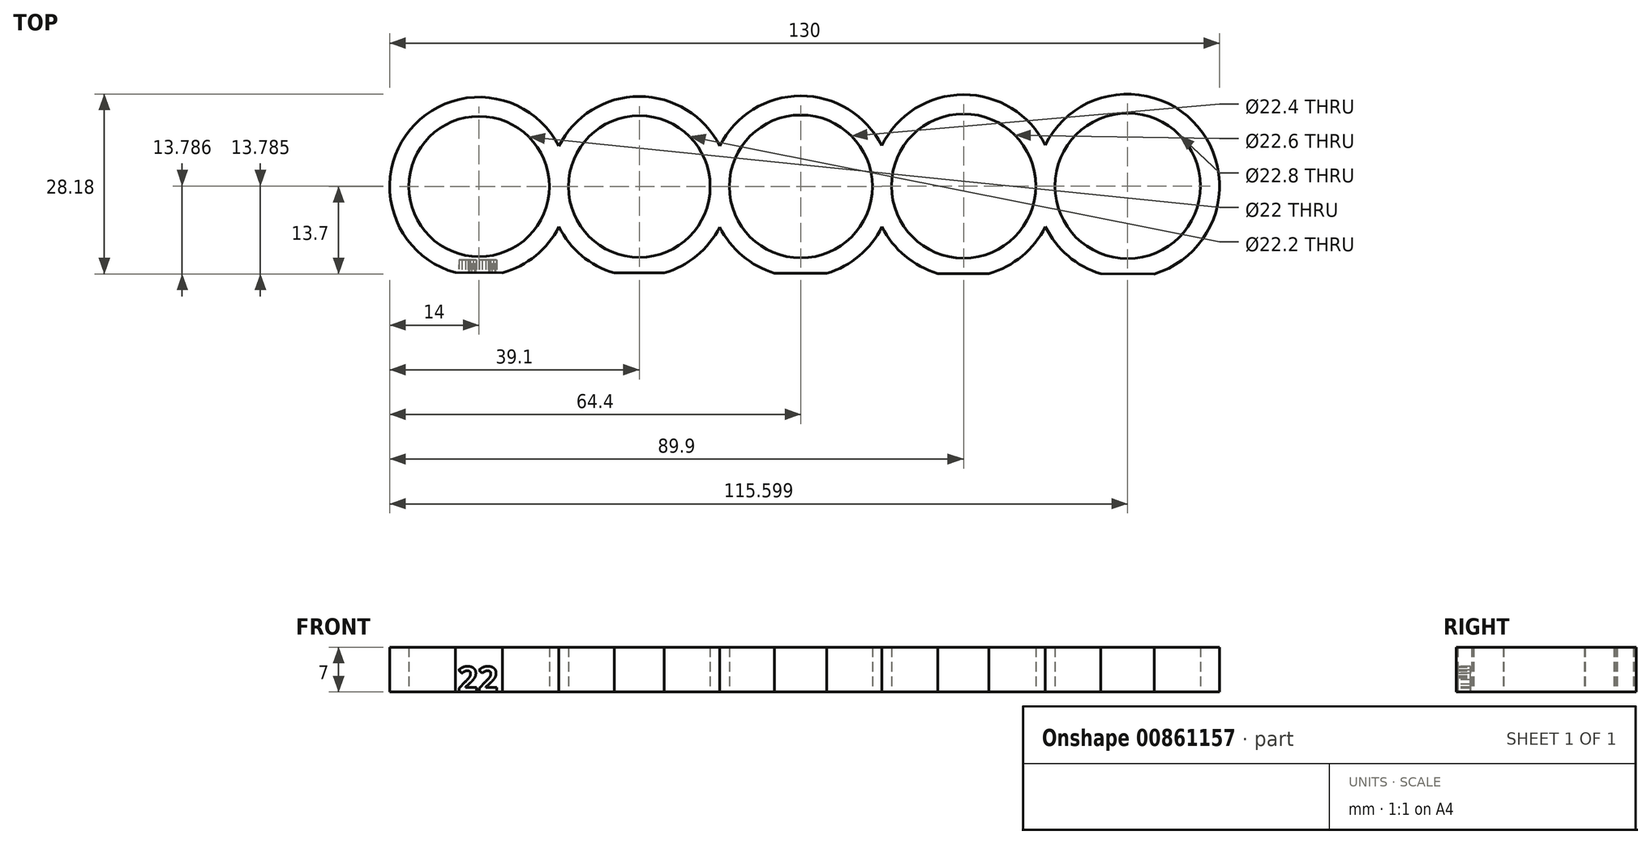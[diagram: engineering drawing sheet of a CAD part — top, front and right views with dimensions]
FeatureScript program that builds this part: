
annotation { "Feature Type Name" : "Feature", "Feature Type Description" : "" }
export const myFeature = defineFeature(function(context is Context, id is Id, definition is map)
    precondition{}
    {
        {
            var Q0;
            Q0=qCreatedBy(makeId("Top.planeOp"),FACE);
            var sketch = newSketch(context, id + "F0", { "sketchPlane" : qUnion([Q0])});
            skCircle(sketch, "E0", {"center": v(0, 0) * mm, "radius": 11.2 * mm});
            skCircle(sketch, "E1", {"center": v(25.5, 0.09) * mm, "radius": 11.3 * mm});
            skCircle(sketch, "E2", {"center": v(51.2, 0.08) * mm, "radius": 11.4 * mm});
            skCircle(sketch, "E3", {"center": v(-50.4, 0) * mm, "radius": 11 * mm});
            skCircle(sketch, "E4", {"center": v(-25.3, 0) * mm, "radius": 11.1 * mm});
            skLineSegment(sketch, "E5", {"start": v(-14.7, 0) * mm, "end": v(-14.2, 0) * mm, "construction": true});
            skLineSegment(sketch, "E6", {"start": v(-39.45, 0) * mm, "end": v(-39.4, 0) * mm, "construction": true});
            skLineSegment(sketch, "E7", {"start": v(39.8, 0) * mm, "end": v(40.1, 0) * mm, "construction": true});
            skArc(sketch, "E8.0", {"start": v(-37.9, 6.32) * mm, "mid": v(-64.4, 0) * mm, "end": v(-37.9, -6.32) * mm});
            skArc(sketch, "E9.0", {"start": v(-37.9, -6.32) * mm, "mid": v(-25.31, -14.1) * mm, "end": v(-12.7, -6.34) * mm});
            skArc(sketch, "E10.0", {"start": v(-12.7, -6.34) * mm, "mid": v(0.01, -14.2) * mm, "end": v(12.72, -6.32) * mm});
            skArc(sketch, "E11.0", {"start": v(11.2, 0.08) * mm, "mid": v(11.2, 0.04) * mm, "end": v(11.2, 0) * mm});
            skArc(sketch, "E12.0", {"start": v(36.8, 0.18) * mm, "mid": v(36.8, 0.09) * mm, "end": v(36.8, 0) * mm});
            skArc(sketch, "E13.trimOffspring", {"start": v(-12.7, 6.34) * mm, "mid": v(-25.31, 14.1) * mm, "end": v(-37.9, 6.32) * mm});
            skArc(sketch, "E14.trimOffspring", {"start": v(12.67, 6.4) * mm, "mid": v(-0.04, 14.2) * mm, "end": v(-12.7, 6.34) * mm});
            skPoint(sketch, "E15.start.orphan", {"position": v(11.2, 0) * mm});
            skArc(sketch, "E16.trimOffspring", {"start": v(12.72, -6.32) * mm, "mid": v(25.51, -14.21) * mm, "end": v(38.3, -6.3) * mm});
            skArc(sketch, "E17.trimOffspring", {"start": v(14.2, 0.01) * mm, "mid": v(14.2, 0.05) * mm, "end": v(14.2, 0.09) * mm});
            skArc(sketch, "E18.trimOffspring", {"start": v(38.3, 6.47) * mm, "mid": v(25.46, 14.39) * mm, "end": v(12.67, 6.4) * mm});
            skArc(sketch, "E19.trimOffspring", {"start": v(38.3, -6.3) * mm, "mid": v(65.6, 0.08) * mm, "end": v(38.3, 6.47) * mm});
            skArc(sketch, "E20.trimOffspring", {"start": v(39.8, 0) * mm, "mid": v(39.8, 0.09) * mm, "end": v(39.8, 0.18) * mm});
            skSolve(sketch);
        }
        {
            var Q0;
            Q0 = qSketchRegion(id + "F0", true);
            extrude(context, id + "F1", {"entities" : qUnion([Q0]), "depth" : 7 * mm, "offsetDistance" : 25 * mm});
        }
        {
            var Q0;
            Q0=makeQuery(id+"F1.opExtrude","CAP_FACE",FACE,{"disambiguationData":[OSD([sQuery(id+"F0.wireOp",EDGE,"E0"),sQuery(id+"F0.wireOp",EDGE,"E1"),sQuery(id+"F0.wireOp",EDGE,"E2"),sQuery(id+"F0.wireOp",EDGE,"E3"),sQuery(id+"F0.wireOp",EDGE,"E4"),sQuery(id+"F0.wireOp",EDGE,"E8.0"),sQuery(id+"F0.wireOp",EDGE,"E9.0"),sQuery(id+"F0.wireOp",EDGE,"E10.0"),sQuery(id+"F0.wireOp",EDGE,"E13.trimOffspring"),sQuery(id+"F0.wireOp",EDGE,"E14.trimOffspring"),sQuery(id+"F0.wireOp",EDGE,"E16.trimOffspring"),sQuery(id+"F0.wireOp",EDGE,"E18.trimOffspring"),sQuery(id+"F0.wireOp",EDGE,"E19.trimOffspring")])],"isStart":false});
            var sketch = newSketch(context, id + "F2", { "sketchPlane" : qUnion([Q0])});
            skLineSegment(sketch, "E21", {"start": v(-50.4, -14) * mm, "end": v(-50.4, -13.5) * mm, "construction": true});
            skLineSegment(sketch, "E22", {"start": v(-25.3, -14.1) * mm, "end": v(-25.3, -13.6) * mm, "construction": true});
            skPoint(sketch, "E22.startSnap0", {"position": v(-25.31, -14.1) * mm});
            skLineSegment(sketch, "E23", {"start": v(0.01, -14.2) * mm, "end": v(0.01, -13.7) * mm, "construction": true});
            skPoint(sketch, "E23.startSnap0", {"position": v(0.01, -14.2) * mm});
            skLineSegment(sketch, "E24", {"start": v(25.51, -14.21) * mm, "end": v(25.51, -13.71) * mm, "construction": true});
            skLineSegment(sketch, "E25", {"start": v(52.9, -14.21) * mm, "end": v(52.9, -13.71) * mm, "construction": true});
            skLineSegment(sketch, "E26", {"start": v(-50.4, -13.5) * mm, "end": v(63.83, -13.71) * mm});
            skLineSegment(sketch, "E27", {"start": v(-50.4, -13.5) * mm, "end": v(-55.8, -13.49) * mm});
            skLineSegment(sketch, "E28", {"start": v(-55.8, -13.49) * mm, "end": v(-55.8, -17.63) * mm});
            skLineSegment(sketch, "E29", {"start": v(-55.8, -17.63) * mm, "end": v(63.83, -17.85) * mm});
            skLineSegment(sketch, "E30", {"start": v(63.83, -17.85) * mm, "end": v(63.83, -13.71) * mm});
            skSolve(sketch);
        }
        {
            var Q0;
            Q0 = qSketchRegion(id + "F2", true);
            extrude(context, id + "F3", {"entities" : qUnion([Q0]), "operationType" : NewBodyOperationType.REMOVE, "oppositeDirection" : true, "depth" : 25 * mm, "offsetDistance" : 25 * mm});
        }
        {
            var Q0;
            {var subQ7=sQuery(id+"F0.wireOp",EDGE,"E8.0");Q0=makeQuery(id+"F3.boolean.opBoolean","COPY",FACE,{"disambiguationData":[TD([makeQuery(id+"F1.opExtrude","SWEPT_FACE",FACE,{"disambiguationData":[OSD([subQ7])]})])],"derivedFrom":makeQuery(id+"F3.opExtrude","SWEPT_FACE",FACE,{"disambiguationData":[OSD([sQuery(id+"F2.wireOp",EDGE,"E26"),sQuery(id+"F2.wireOp",EDGE,"E27")])]})});}
            var sketch = newSketch(context, id + "F4", { "sketchPlane" : qUnion([Q0])});
            skLineSegment(sketch, "E31.bottom", {"start": v(-41.37, -12.98) * mm, "end": v(-26.4, -12.98) * mm});
            skLineSegment(sketch, "E31.top", {"start": v(-41.37, -1.66) * mm, "end": v(-26.4, -1.66) * mm});
            skLineSegment(sketch, "E31.left", {"start": v(-41.37, -12.98) * mm, "end": v(-41.37, -1.66) * mm});
            skLineSegment(sketch, "E31.right", {"start": v(-26.4, -12.98) * mm, "end": v(-26.4, -1.66) * mm});
            skText(sketch, "E32", { "text": "22", "fontName": "OpenSans-Bold.ttf"});
            const initialGuessF4  = {"E32": [-0.05376, 0, 1, 0, 0.004]};
            skSetInitialGuess(sketch, initialGuessF4);
            skSolve(sketch);
        }
        {
            var Q0;
            Q0=makeQuery(id+"F4.imprint","IMPRINT",FACE,{"disambiguationData":[TD([[makeQuery(id+"F4.imprint","IMPRINT",EDGE,{"derivedFrom":sQuery(id+"F4.wireOp",EDGE,"E32.sketch_text.stroke-0")}),1.0]])]});
            var Q1;
            Q1=makeQuery(id+"F4.imprint","IMPRINT",FACE,{"disambiguationData":[TD([[makeQuery(id+"F4.imprint","IMPRINT",EDGE,{"derivedFrom":sQuery(id+"F4.wireOp",EDGE,"E32.sketch_text.stroke-24")}),1.0]])]});
            extrude(context, id + "F5", {"entities" : qUnion([Q0, Q1]), "operationType" : NewBodyOperationType.REMOVE, "oppositeDirection" : true, "depth" : 2 * mm, "offsetDistance" : 25 * mm});
        }
    });
